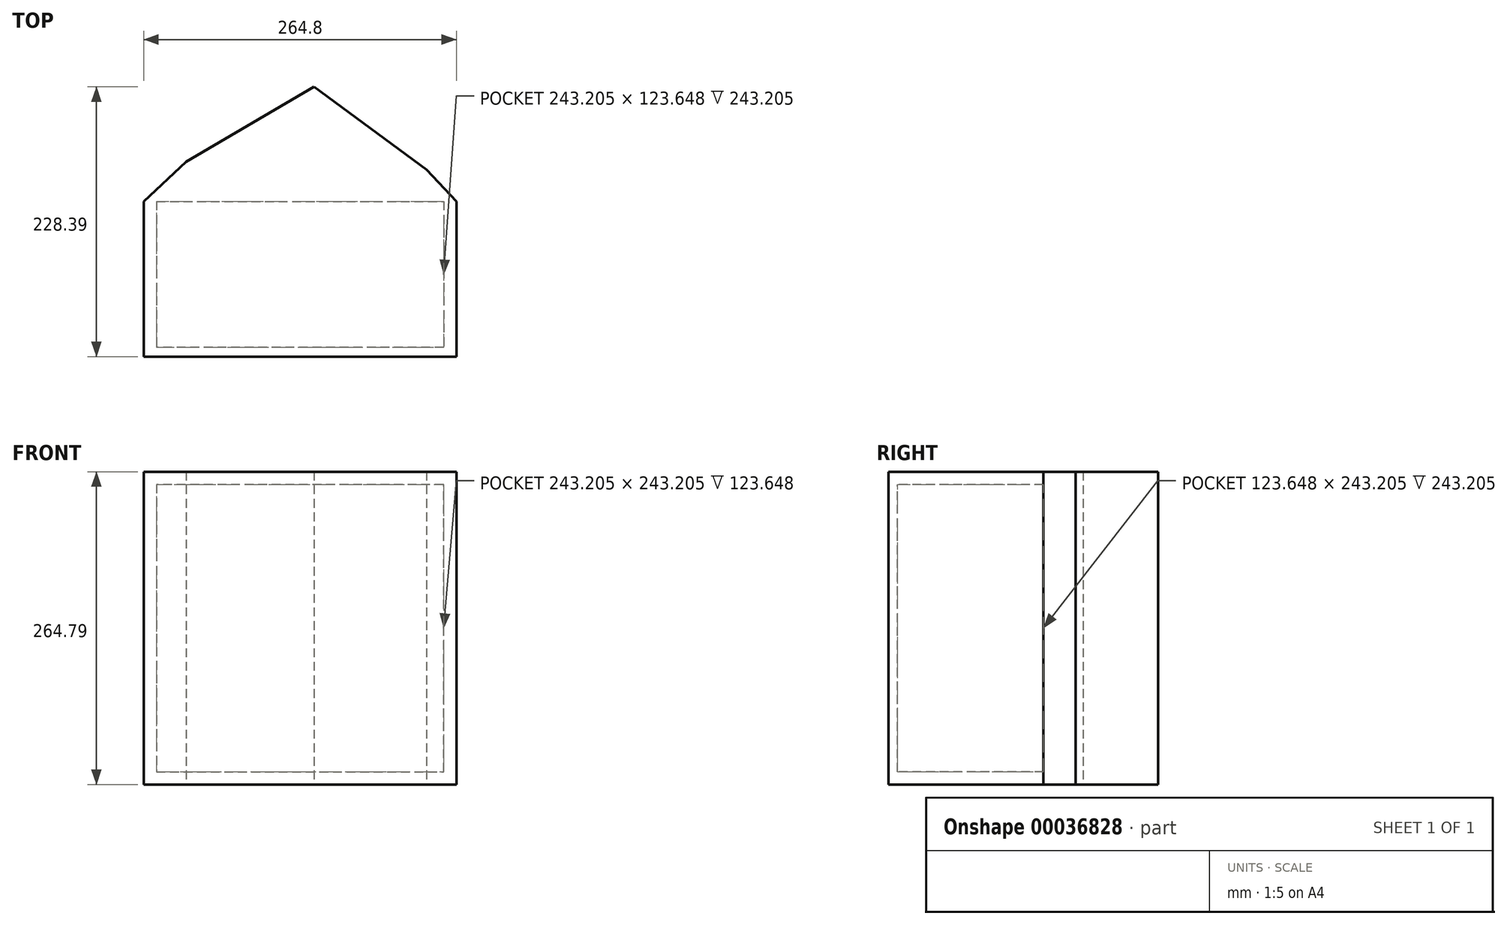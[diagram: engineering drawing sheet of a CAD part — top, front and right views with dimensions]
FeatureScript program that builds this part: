
annotation { "Feature Type Name" : "Feature", "Feature Type Description" : "" }
export const myFeature = defineFeature(function(context is Context, id is Id, definition is map)
    precondition{}
    {
        {
            var Q0;
            Q0=qCreatedBy(makeId("Top.planeOp"),FACE);
            var sketch = newSketch(context, id + "F0", { "sketchPlane" : qUnion([Q0])});
            skLineSegment(sketch, "E0.rect.bottom", {"start": v(5.4, 65.67) * mm, "end": v(-5.4, 65.67) * mm});
            skLineSegment(sketch, "E0.rect.top", {"start": v(5.4, -65.67) * mm, "end": v(-5.4, -65.67) * mm});
            skLineSegment(sketch, "E0.rect.left", {"start": v(5.4, 65.67) * mm, "end": v(5.4, -65.67) * mm});
            skLineSegment(sketch, "E0.rect.right", {"start": v(-5.4, 65.67) * mm, "end": v(-5.4, -65.67) * mm});
            skPoint(sketch, "E0.rect.middle", {"position": v(0, 0) * mm});
            skSolve(sketch);
        }
        {
            var Q0;
            Q0=makeQuery(id+"F0.imprint","IMPRINT",FACE,{"disambiguationData":[TD([[makeQuery(id+"F0.imprint","IMPRINT",EDGE,{"derivedFrom":sQuery(id+"F0.wireOp",EDGE,"E0.rect.bottom")}),1.0]])]});
            extrude(context, id + "F1", {"entities" : qUnion([Q0]), "depth" : 127 * mm, "hasSecondDirection" : true, "secondDirectionOppositeDirection" : true, "secondDirectionDepth" : 127 * mm});
        }
        {
            var Q0;
            Q0=makeQuery(id+"F1.opExtrude","SWEPT_FACE",FACE,{"disambiguationData":[OSD([sQuery(id+"F0.wireOp",EDGE,"E0.rect.left")])]});
            var sketch = newSketch(context, id + "F2", { "sketchPlane" : qUnion([Q0])});
            skLineSegment(sketch, "E1.bottom", {"start": v(65.67, 127) * mm, "end": v(-65.67, 127) * mm});
            skLineSegment(sketch, "E1.top", {"start": v(65.67, 116.2) * mm, "end": v(-65.67, 116.2) * mm});
            skLineSegment(sketch, "E1.left", {"start": v(65.67, 127) * mm, "end": v(65.67, 116.2) * mm});
            skLineSegment(sketch, "E1.right", {"start": v(-65.67, 127) * mm, "end": v(-65.67, 116.2) * mm});
            skSolve(sketch);
        }
        {
            var Q0;
            Q0 = qSketchRegion(id + "F2", true);
            extrude(context, id + "F3", {"entities" : qUnion([Q0]), "operationType" : NewBodyOperationType.ADD, "depth" : 254 * mm});
        }
        {
            var Q0;
            Q0=makeQuery(id+"F3.opExtrude","SWEPT_FACE",FACE,{"disambiguationData":[OSD([sQuery(id+"F2.wireOp",EDGE,"E1.top")])]});
            var sketch = newSketch(context, id + "F4", { "sketchPlane" : qUnion([Q0])});
            skLineSegment(sketch, "E2.bottom", {"start": v(259.4, -65.67) * mm, "end": v(248.6, -65.67) * mm});
            skLineSegment(sketch, "E2.top", {"start": v(259.4, 65.67) * mm, "end": v(248.6, 65.67) * mm});
            skLineSegment(sketch, "E2.left", {"start": v(259.4, -65.67) * mm, "end": v(259.4, 65.67) * mm});
            skLineSegment(sketch, "E2.right", {"start": v(248.6, -65.67) * mm, "end": v(248.6, 65.67) * mm});
            skSolve(sketch);
        }
        {
            var Q0;
            Q0 = qSketchRegion(id + "F4", true);
            extrude(context, id + "F5", {"entities" : qUnion([Q0]), "operationType" : NewBodyOperationType.ADD, "depth" : 254 * mm});
        }
        {
            var Q0;
            Q0=makeQuery(id+"F5.opExtrude","SWEPT_FACE",FACE,{"disambiguationData":[OSD([sQuery(id+"F4.wireOp",EDGE,"E2.right")])]});
            var sketch = newSketch(context, id + "F6", { "sketchPlane" : qUnion([Q0])});
            skLineSegment(sketch, "E3.bottom", {"start": v(65.67, -137.8) * mm, "end": v(-65.67, -137.8) * mm});
            skLineSegment(sketch, "E3.top", {"start": v(65.67, -127) * mm, "end": v(-65.67, -127) * mm});
            skLineSegment(sketch, "E3.left", {"start": v(65.67, -137.8) * mm, "end": v(65.67, -127) * mm});
            skLineSegment(sketch, "E3.right", {"start": v(-65.67, -137.8) * mm, "end": v(-65.67, -127) * mm});
            skSolve(sketch);
        }
        {
            var Q0;
            Q0 = qSketchRegion(id + "F6", true);
            extrude(context, id + "F7", {"entities" : qUnion([Q0]), "operationType" : NewBodyOperationType.ADD, "depth" : 254 * mm});
        }
        {
            var Q0;
            Q0=makeQuery(id+"F5.boolean.opBoolean","MERGE",FACE,{"derivedFrom":[makeQuery(id+"F3.opExtrude","CAP_FACE",FACE,{"disambiguationData":[OSD([sQuery(id+"F2.wireOp",EDGE,"E1.bottom"),sQuery(id+"F2.wireOp",EDGE,"E1.top"),sQuery(id+"F2.wireOp",EDGE,"E1.left"),sQuery(id+"F2.wireOp",EDGE,"E1.right")])],"isStart":false}),makeQuery(id+"F5.opExtrude","SWEPT_FACE",FACE,{"disambiguationData":[OSD([sQuery(id+"F4.wireOp",EDGE,"E2.left")])]})]});
            var sketch = newSketch(context, id + "F8", { "sketchPlane" : qUnion([Q0])});
            skLineSegment(sketch, "E4.bottom", {"start": v(-65.67, 127) * mm, "end": v(-57.97, 127) * mm});
            skLineSegment(sketch, "E4.top", {"start": v(-65.67, -137.8) * mm, "end": v(-57.97, -137.8) * mm});
            skLineSegment(sketch, "E4.left", {"start": v(-65.67, 127) * mm, "end": v(-65.67, -137.8) * mm});
            skLineSegment(sketch, "E4.right", {"start": v(-57.97, 127) * mm, "end": v(-57.97, -137.8) * mm});
            skSolve(sketch);
        }
        {
            var Q0;
            Q0 = qSketchRegion(id + "F8", true);
            extrude(context, id + "F9", {"entities" : qUnion([Q0]), "operationType" : NewBodyOperationType.ADD, "oppositeDirection" : true, "depth" : 254 * mm});
        }
        {
            var Q0;
            Q0=makeQuery(id+"F7.boolean.opBoolean","MERGE",FACE,{"derivedFrom":[makeQuery(id+"F5.opExtrude","CAP_FACE",FACE,{"disambiguationData":[OSD([sQuery(id+"F4.wireOp",EDGE,"E2.bottom"),sQuery(id+"F4.wireOp",EDGE,"E2.top"),sQuery(id+"F4.wireOp",EDGE,"E2.left"),sQuery(id+"F4.wireOp",EDGE,"E2.right")])],"isStart":false}),makeQuery(id+"F7.opExtrude","SWEPT_FACE",FACE,{"disambiguationData":[OSD([sQuery(id+"F6.wireOp",EDGE,"E3.bottom")])]})]});
            var sketch = newSketch(context, id + "F10", { "sketchPlane" : qUnion([Q0])});
            skLineSegment(sketch, "E5", {"start": v(259.4, -65.67) * mm, "end": v(234, -92.7) * mm});
            skLineSegment(sketch, "E6", {"start": v(234, -92.7) * mm, "end": v(138.86, -162.72) * mm});
            skLineSegment(sketch, "E7", {"start": v(138.86, -162.72) * mm, "end": v(30.55, -99.3) * mm});
            skLineSegment(sketch, "E8", {"start": v(30.55, -99.3) * mm, "end": v(-5.4, -65.67) * mm});
            skLineSegment(sketch, "E9", {"start": v(259.4, -65.67) * mm, "end": v(-5.4, -65.67) * mm});
            skSolve(sketch);
        }
        {
            var Q0;
            Q0 = qSketchRegion(id + "F10", true);
            extrude(context, id + "F11", {"entities" : qUnion([Q0]), "operationType" : NewBodyOperationType.ADD, "oppositeDirection" : true, "depth" : 264.8 * mm});
        }
    });
